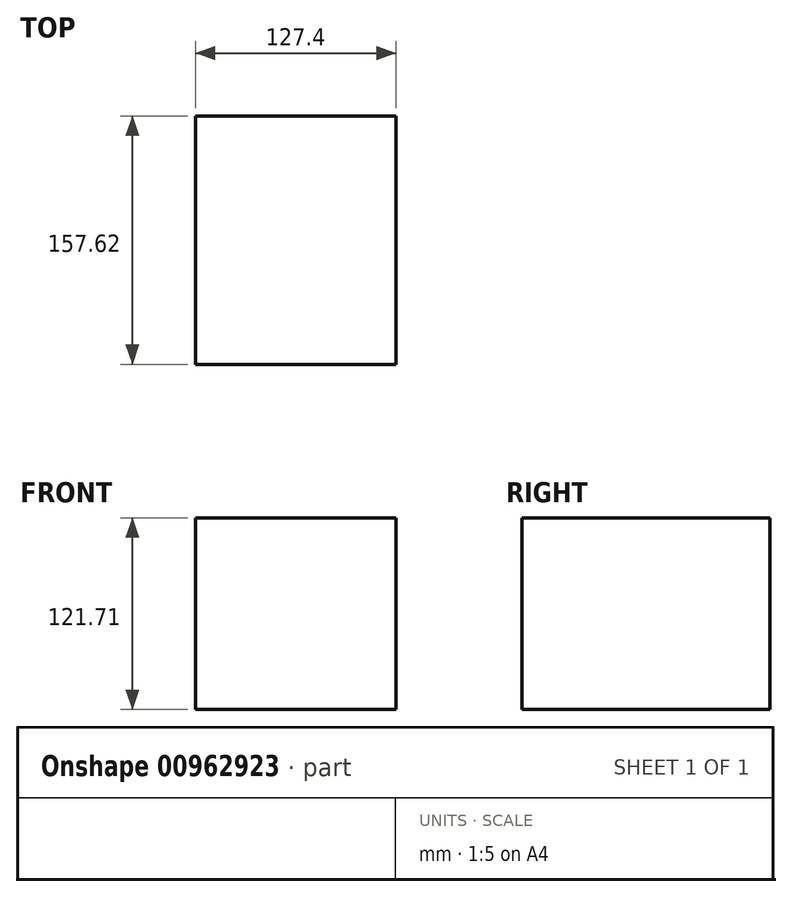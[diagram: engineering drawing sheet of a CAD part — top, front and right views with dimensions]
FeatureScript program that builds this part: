
annotation { "Feature Type Name" : "Feature", "Feature Type Description" : "" }
export const myFeature = defineFeature(function(context is Context, id is Id, definition is map)
    precondition{}
    {
        {
            var Q0;
            Q0=qCreatedBy(makeId("Front.planeOp"),FACE);
            var sketch = newSketch(context, id + "F0", { "sketchPlane" : qUnion([Q0])});
            skLineSegment(sketch, "E0.bottom", {"start": v(51.8, -23.46) * mm, "end": v(-75.6, -23.46) * mm});
            skLineSegment(sketch, "E0.top", {"start": v(51.8, 98.25) * mm, "end": v(-75.6, 98.25) * mm});
            skLineSegment(sketch, "E0.left", {"start": v(51.8, -23.46) * mm, "end": v(51.8, 98.25) * mm});
            skLineSegment(sketch, "E0.right", {"start": v(-75.6, -23.46) * mm, "end": v(-75.6, 98.25) * mm});
            skPoint(sketch, "E0.middle", {"position": v(-11.9, 37.4) * mm});
            skSolve(sketch);
        }
        {
            var Q0;
            Q0=makeQuery(id+"F0.imprint","IMPRINT",FACE,{"disambiguationData":[TD([[makeQuery(id+"F0.imprint","IMPRINT",EDGE,{"derivedFrom":sQuery(id+"F0.wireOp",EDGE,"E0.bottom")}),-1.0]])]});
            extrude(context, id + "F1", {"entities" : qUnion([Q0]), "depth" : 157.62 * mm, "offsetDistance" : 25.4 * mm});
        }
    });
